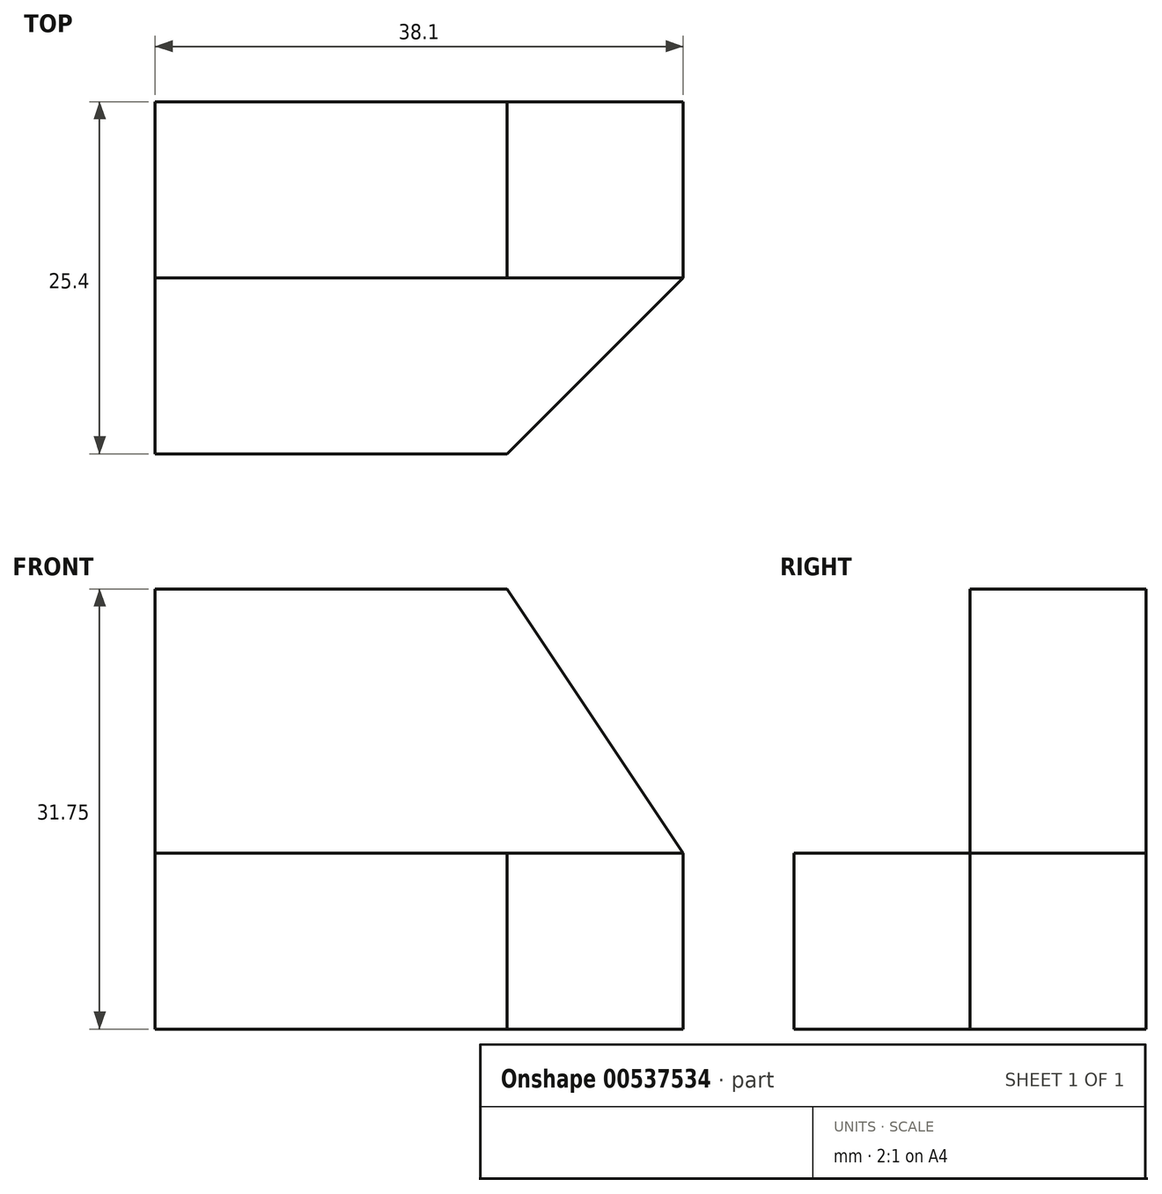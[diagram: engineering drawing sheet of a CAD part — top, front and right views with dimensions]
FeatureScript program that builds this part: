
annotation { "Feature Type Name" : "Feature", "Feature Type Description" : "" }
export const myFeature = defineFeature(function(context is Context, id is Id, definition is map)
    precondition{}
    {
        {
            var Q0;
            Q0=qCreatedBy(makeId("Right.planeOp"),FACE);
            var sketch = newSketch(context, id + "F0", { "sketchPlane" : qUnion([Q0])});
            skLineSegment(sketch, "E0", {"start": v(0, 0) * mm, "end": v(0, 31.75) * mm});
            skLineSegment(sketch, "E1", {"start": v(0, 31.75) * mm, "end": v(-12.7, 31.75) * mm});
            skLineSegment(sketch, "E2", {"start": v(-12.7, 31.75) * mm, "end": v(-12.7, 12.7) * mm});
            skLineSegment(sketch, "E3", {"start": v(-12.7, 12.7) * mm, "end": v(-25.4, 12.7) * mm});
            skLineSegment(sketch, "E4", {"start": v(-25.4, 12.7) * mm, "end": v(-25.4, 0) * mm});
            skLineSegment(sketch, "E5", {"start": v(-25.4, 0) * mm, "end": v(0, 0) * mm});
            skSolve(sketch);
        }
        {
            var Q0;
            Q0 = qSketchRegion(id + "F0", true);
            extrude(context, id + "F1", {"entities" : qUnion([Q0]), "depth" : 38.1 * mm, "offsetDistance" : 25.4 * mm});
        }
        {
            var Q0;
            Q0=makeQuery(id+"F1.opExtrude","SWEPT_FACE",FACE,{"disambiguationData":[OSD([sQuery(id+"F0.wireOp",EDGE,"E3")])]});
            var sketch = newSketch(context, id + "F2", { "sketchPlane" : qUnion([Q0])});
            skLineSegment(sketch, "E6", {"start": v(25.4, -25.4) * mm, "end": v(38.1, -12.7) * mm});
            skLineSegment(sketch, "E7", {"start": v(25.4, -25.4) * mm, "end": v(38.1, -25.4) * mm});
            skLineSegment(sketch, "E8", {"start": v(38.1, -25.4) * mm, "end": v(38.1, -12.7) * mm});
            skSolve(sketch);
        }
        {
            var Q0;
            Q0=makeQuery(id+"F2.imprint","IMPRINT",FACE,{"disambiguationData":[TD([[makeQuery(id+"F2.imprint","IMPRINT",EDGE,{"derivedFrom":sQuery(id+"F2.wireOp",EDGE,"E6")}),-1.0]])]});
            extrude(context, id + "F3", {"entities" : qUnion([Q0]), "operationType" : NewBodyOperationType.REMOVE, "oppositeDirection" : true, "depth" : 25.4 * mm, "offsetDistance" : 25.4 * mm});
        }
        {
            var Q0;
            Q0=makeQuery(id+"F1.opExtrude","SWEPT_FACE",FACE,{"disambiguationData":[OSD([sQuery(id+"F0.wireOp",EDGE,"E2")])]});
            var sketch = newSketch(context, id + "F4", { "sketchPlane" : qUnion([Q0])});
            skLineSegment(sketch, "E9", {"start": v(25.4, 31.75) * mm, "end": v(38.1, 12.7) * mm});
            skSolve(sketch);
        }
        {
            var Q0;
            {var subQ0=sQuery(id+"F4.wireOp",EDGE,"E9");Q0=makeQuery(id+"F4.imprint","IMPRINT",FACE,{"disambiguationData":[TD([[makeQuery(id+"F4.imprint","IMPRINT",EDGE,{"derivedFrom":subQ0}),1.0]])]});}
            extrude(context, id + "F5", {"entities" : qUnion([Q0]), "operationType" : NewBodyOperationType.REMOVE, "oppositeDirection" : true, "depth" : 25.4 * mm, "offsetDistance" : 25.4 * mm});
        }
    });
